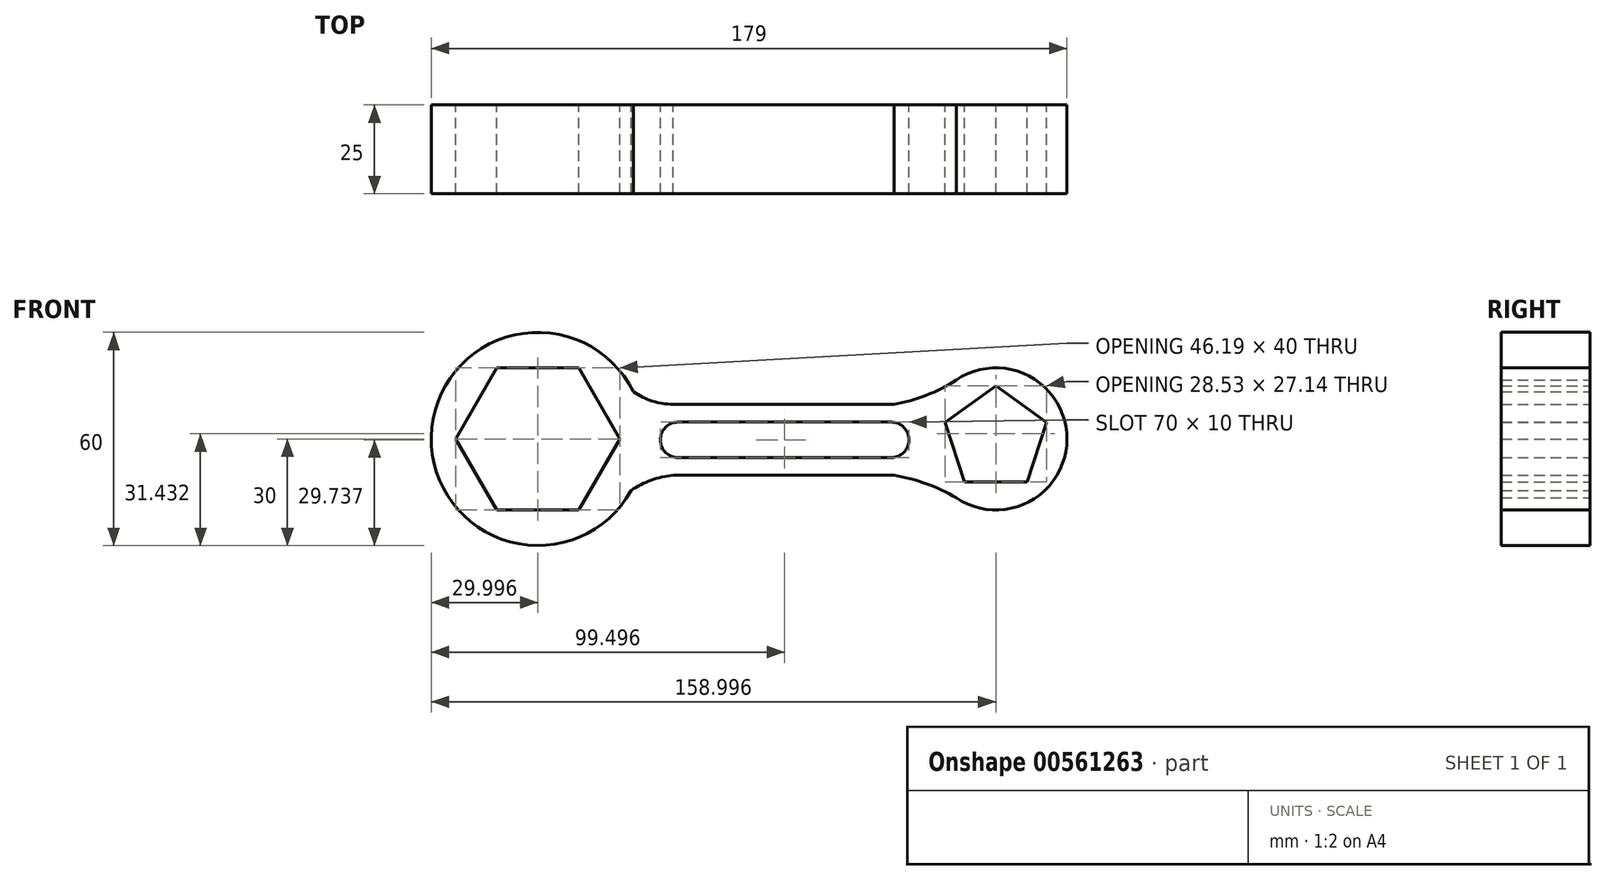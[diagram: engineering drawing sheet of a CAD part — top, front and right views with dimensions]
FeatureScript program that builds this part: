
annotation { "Feature Type Name" : "Feature", "Feature Type Description" : "" }
export const myFeature = defineFeature(function(context is Context, id is Id, definition is map)
    precondition{}
    {
        {
            var Q0;
            Q0=qCreatedBy(makeId("Front.planeOp"),FACE);
            var sketch = newSketch(context, id + "F0", { "sketchPlane" : qUnion([Q0])});
            skCircle(sketch, "E0", {"center": v(-75.32, 0) * mm, "radius": 30 * mm});
            skCircle(sketch, "E1", {"center": v(53.68, 0) * mm, "radius": 20 * mm});
            skCircle(sketch, "E2.cCircle", {"center": v(-75.32, 0) * mm, "radius": 20 * mm, "construction": true});
            skLineSegment(sketch, "E2.0", {"start": v(-86.87, 20) * mm, "end": v(-63.78, 20) * mm});
            skLineSegment(sketch, "E2.1", {"start": v(-63.78, 20) * mm, "end": v(-52.23, 0) * mm});
            skLineSegment(sketch, "E2.2", {"start": v(-52.23, 0) * mm, "end": v(-63.78, -20) * mm});
            skLineSegment(sketch, "E2.3", {"start": v(-63.78, -20) * mm, "end": v(-86.87, -20) * mm});
            skLineSegment(sketch, "E2.4", {"start": v(-86.87, -20) * mm, "end": v(-98.42, 0) * mm});
            skLineSegment(sketch, "E2.5", {"start": v(-98.42, 0) * mm, "end": v(-86.87, 20) * mm});
            skPoint(sketch, "E2.0.midPoint", {"position": v(-75.32, 20) * mm});
            skCircle(sketch, "E3.cCircle", {"center": v(53.68, 0) * mm, "radius": 15 * mm, "construction": true});
            skLineSegment(sketch, "E3.0", {"start": v(67.94, 4.64) * mm, "end": v(53.68, 15) * mm});
            skLineSegment(sketch, "E3.1", {"start": v(62.5, -12.14) * mm, "end": v(67.94, 4.64) * mm});
            skLineSegment(sketch, "E3.2", {"start": v(44.86, -12.14) * mm, "end": v(62.5, -12.14) * mm});
            skLineSegment(sketch, "E3.3", {"start": v(39.41, 4.64) * mm, "end": v(44.86, -12.14) * mm});
            skLineSegment(sketch, "E3.4", {"start": v(53.68, 15) * mm, "end": v(39.41, 4.64) * mm});
            skLineSegment(sketch, "E4", {"start": v(24.94, 9.74) * mm, "end": v(-37.21, 9.74) * mm});
            skLineSegment(sketch, "E5", {"start": v(24.94, -10.26) * mm, "end": v(-37.21, -10.26) * mm});
            skArc(sketch, "E6", {"start": v(-48.45, 13.34) * mm, "mid": v(-43.12, 10.66) * mm, "end": v(-37.21, 9.74) * mm});
            skArc(sketch, "E7", {"start": v(24.94, 9.74) * mm, "mid": v(34.06, 12.3) * mm, "end": v(42.5, 16.6) * mm});
            skArc(sketch, "E8", {"start": v(42.5, -16.6) * mm, "mid": v(34.03, -12.57) * mm, "end": v(24.94, -10.26) * mm});
            skArc(sketch, "E9", {"start": v(-37.21, -10.26) * mm, "mid": v(-43.39, -11.64) * mm, "end": v(-49.05, -14.47) * mm});
            skLineSegment(sketch, "E10.bottom", {"start": v(-35.82, 4.74) * mm, "end": v(24.18, 4.74) * mm});
            skLineSegment(sketch, "E10.top", {"start": v(-35.82, -5.26) * mm, "end": v(24.18, -5.26) * mm});
            skLineSegment(sketch, "E10.left", {"start": v(-40.82, -0.26) * mm, "end": v(-40.82, -0.26) * mm});
            skLineSegment(sketch, "E10.right", {"start": v(29.18, -0.26) * mm, "end": v(29.18, -0.26) * mm});
            skPoint(sketch, "E11.visualSharp", {"position": v(-40.82, 4.74) * mm});
            skArc(sketch, "E11.filletArc", {"start": v(-35.82, 4.74) * mm, "mid": v(-39.36, 3.27) * mm, "end": v(-40.82, -0.26) * mm});
            skPoint(sketch, "E12.visualSharp", {"position": v(-40.82, -5.26) * mm});
            skArc(sketch, "E12.filletArc", {"start": v(-40.82, -0.26) * mm, "mid": v(-39.36, -3.8) * mm, "end": v(-35.82, -5.26) * mm});
            skPoint(sketch, "E13.visualSharp", {"position": v(29.18, 4.74) * mm});
            skArc(sketch, "E13.filletArc", {"start": v(29.18, -0.26) * mm, "mid": v(27.71, 3.27) * mm, "end": v(24.18, 4.74) * mm});
            skPoint(sketch, "E14.visualSharp", {"position": v(29.18, -5.26) * mm});
            skArc(sketch, "E14.filletArc", {"start": v(24.18, -5.26) * mm, "mid": v(27.71, -3.8) * mm, "end": v(29.18, -0.26) * mm});
            skSolve(sketch);
        }
        {
            var Q0;
            Q0 = qSketchRegion(id + "F0", true);
            extrude(context, id + "F1", {"entities" : qUnion([Q0]), "depth" : 25 * mm, "offsetDistance" : 25 * mm});
        }
    });
